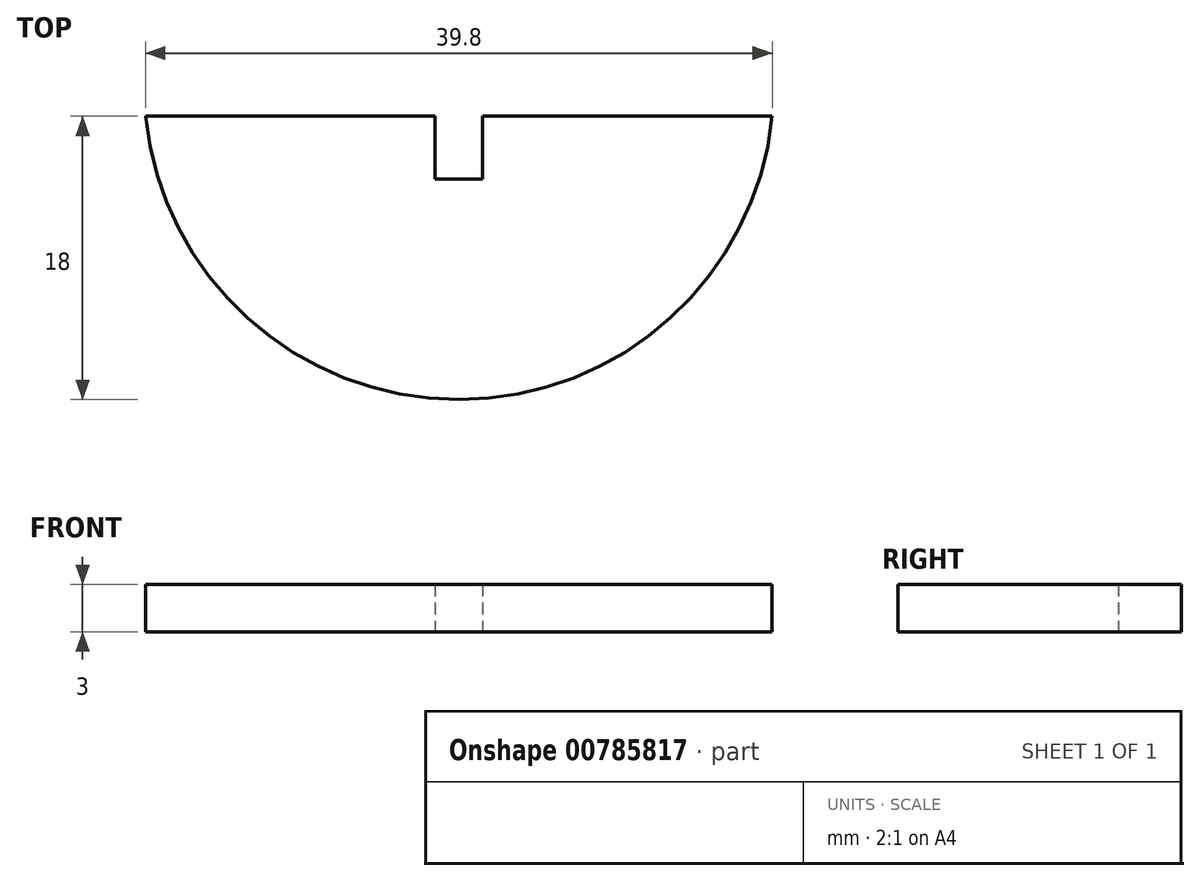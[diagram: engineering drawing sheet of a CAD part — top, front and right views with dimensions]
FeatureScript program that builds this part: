
annotation { "Feature Type Name" : "Feature", "Feature Type Description" : "" }
export const myFeature = defineFeature(function(context is Context, id is Id, definition is map)
    precondition{}
    {
        {
            var Q0;
            Q0=qCreatedBy(makeId("Top.planeOp"),FACE);
            var sketch = newSketch(context, id + "F0", { "sketchPlane" : qUnion([Q0])});
            skArc(sketch, "E0", {"start": v(-20, 0) * mm, "mid": v(0, -20) * mm, "end": v(20, 0) * mm});
            skLineSegment(sketch, "E1", {"start": v(-19.9, -2) * mm, "end": v(19.9, -2) * mm});
            skLineSegment(sketch, "E2", {"start": v(-1.5, 0) * mm, "end": v(-1.5, -6) * mm});
            skLineSegment(sketch, "E3", {"start": v(-1.5, -6) * mm, "end": v(1.5, -6) * mm});
            skLineSegment(sketch, "E4", {"start": v(1.5, -6) * mm, "end": v(1.5, 0) * mm});
            skSolve(sketch);
        }
        {
            var Q0;
            {var subQ0=sQuery(id+"F0.wireOp",EDGE,"E3");Q0=makeQuery(id+"F0.imprint","IMPRINT",FACE,{"disambiguationData":[TD([[makeQuery(id+"F0.imprint","IMPRINT",EDGE,{"derivedFrom":subQ0}),-1.0]])]});}
            extrude(context, id + "F1", {"entities" : qUnion([Q0]), "depth" : 3 * mm, "offsetDistance" : 25 * mm});
        }
    });
